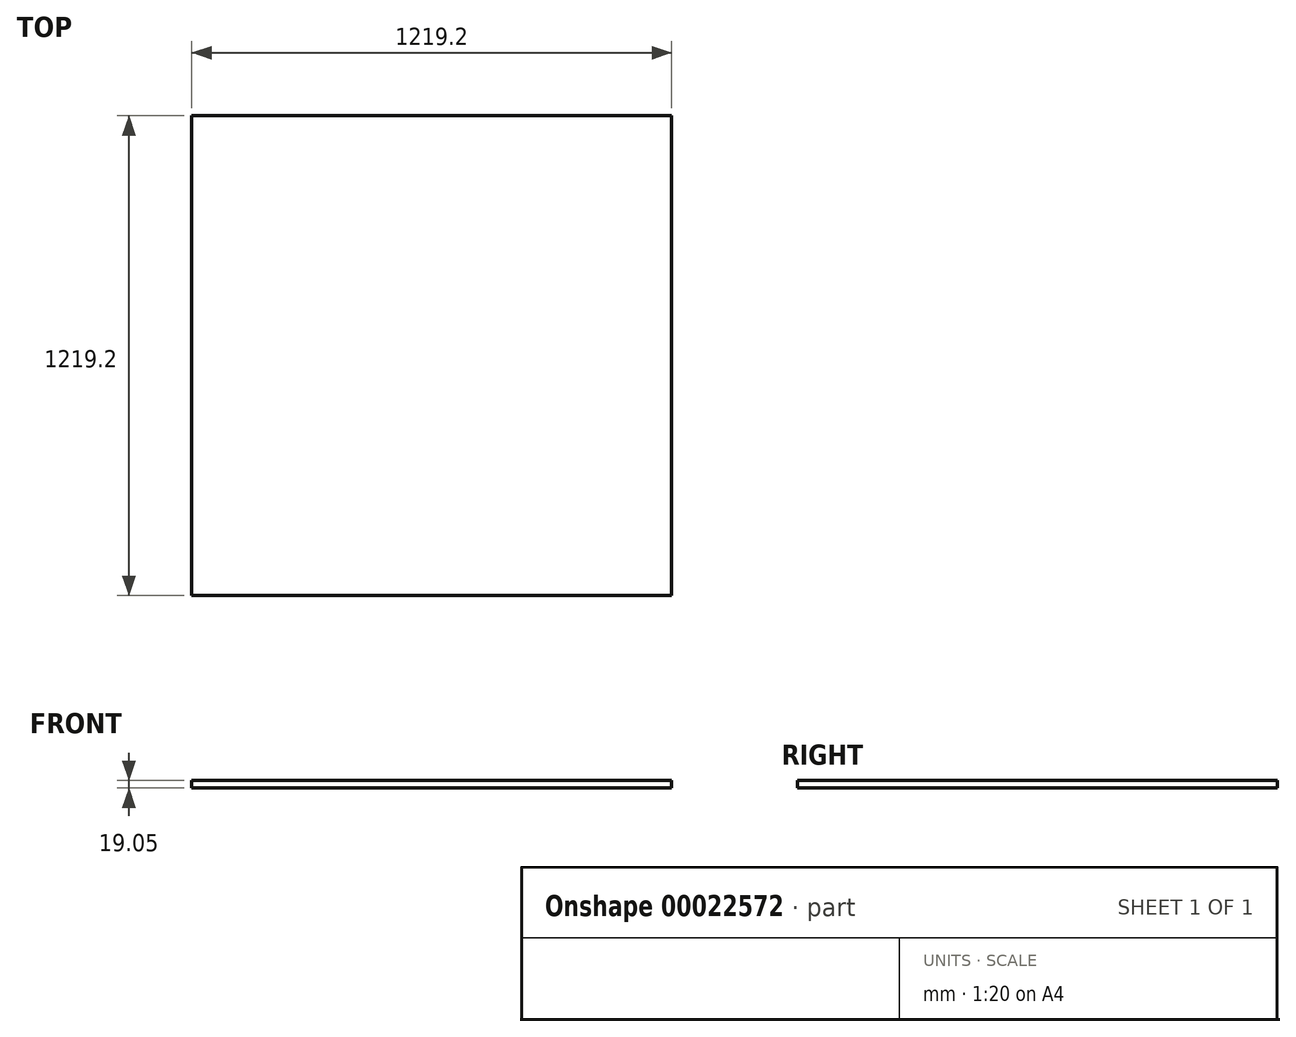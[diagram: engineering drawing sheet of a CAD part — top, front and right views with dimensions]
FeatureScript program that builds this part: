
annotation { "Feature Type Name" : "Feature", "Feature Type Description" : "" }
export const myFeature = defineFeature(function(context is Context, id is Id, definition is map)
    precondition{}
    {
        {
            var Q0;
            Q0=qCreatedBy(makeId("Top.planeOp"),FACE);
            var sketch = newSketch(context, id + "F0", { "sketchPlane" : qUnion([Q0])});
            skLineSegment(sketch, "E0.bottom", {"start": v(0, 0) * mm, "end": v(1219.2, 0) * mm});
            skLineSegment(sketch, "E0.top", {"start": v(0, 1219.2) * mm, "end": v(1219.2, 1219.2) * mm});
            skLineSegment(sketch, "E0.left", {"start": v(0, 0) * mm, "end": v(0, 1219.2) * mm});
            skLineSegment(sketch, "E0.right", {"start": v(1219.2, 0) * mm, "end": v(1219.2, 1219.2) * mm});
            skSolve(sketch);
        }
        {
            var Q0;
            Q0=qSketchRegion(id+"F0",true);
            extrude(context, id + "F1", {"entities" : qUnion([Q0]), "oppositeDirection" : true, "depth" : 19.05 * mm});
        }
    });
